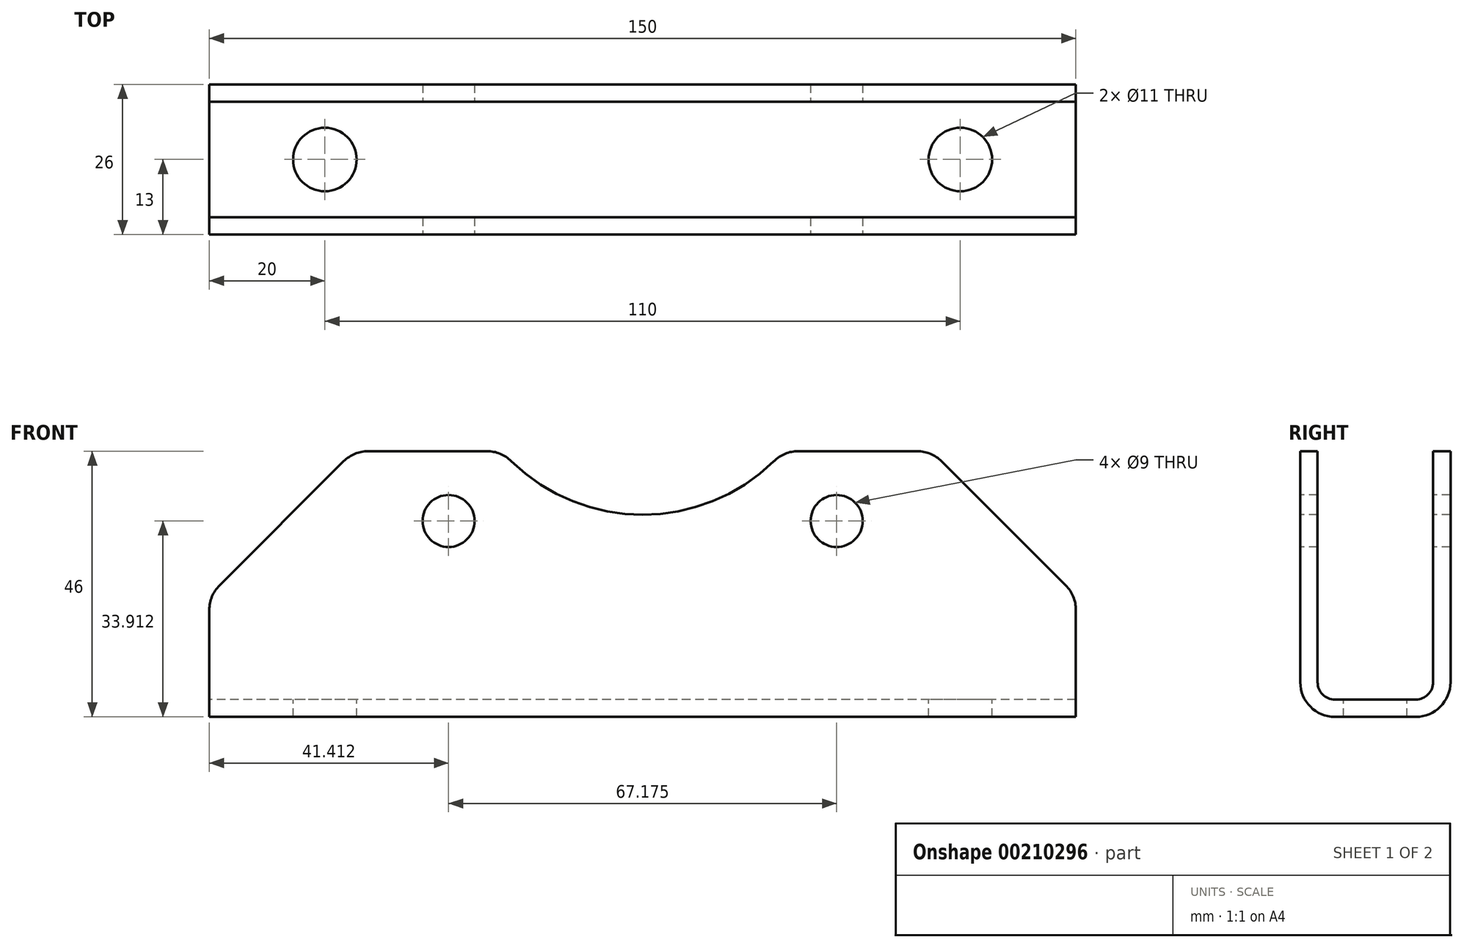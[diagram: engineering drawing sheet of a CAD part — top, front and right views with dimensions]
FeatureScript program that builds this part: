
annotation { "Feature Type Name" : "Feature", "Feature Type Description" : "" }
export const myFeature = defineFeature(function(context is Context, id is Id, definition is map)
    precondition{}
    {
        {
            var Q0;
            Q0=qCreatedBy(makeId("Right.planeOp"),FACE);
            var sketch = newSketch(context, id + "F0", { "sketchPlane" : qUnion([Q0])});
            skLineSegment(sketch, "E0.top", {"start": v(13, -23) * mm, "end": v(-13, -23) * mm});
            skLineSegment(sketch, "E0.left", {"start": v(13, 23) * mm, "end": v(13, -23) * mm});
            skLineSegment(sketch, "E0.right", {"start": v(-13, 23) * mm, "end": v(-13, -23) * mm});
            skPoint(sketch, "E0.middle", {"position": v(0, 0) * mm});
            skLineSegment(sketch, "E1.0", {"start": v(10, 23) * mm, "end": v(10, -20) * mm});
            skLineSegment(sketch, "E1.1", {"start": v(10, -20) * mm, "end": v(-10, -20) * mm});
            skLineSegment(sketch, "E1.2", {"start": v(-10, 23) * mm, "end": v(-10, -20) * mm});
            skLineSegment(sketch, "E2", {"start": v(-13, 23) * mm, "end": v(-10, 23) * mm});
            skLineSegment(sketch, "E3", {"start": v(10, 23) * mm, "end": v(13, 23) * mm});
            skSolve(sketch);
        }
        {
            var Q0;
            Q0=makeQuery(id+"F0.imprint","IMPRINT",FACE,{"disambiguationData":[TD([[makeQuery(id+"F0.imprint","IMPRINT",EDGE,{"derivedFrom":sQuery(id+"F0.wireOp",EDGE,"E0.top")}),-1.0]])]});
            extrude(context, id + "F1", {"entities" : qUnion([Q0]), "depth" : 150 * mm});
        }
        {
            var Q0;
            Q0=makeQuery(id+"F1.opExtrude","SWEPT_FACE",FACE,{"disambiguationData":[OSD([sQuery(id+"F0.wireOp",EDGE,"E0.right")])]});
            var sketch = newSketch(context, id + "F2", { "sketchPlane" : qUnion([Q0])});
            skLineSegment(sketch, "E4", {"start": v(27.5, 44.5) * mm, "end": v(122.5, 44.5) * mm, "construction": true});
            skLineSegment(sketch, "E5", {"start": v(75, -23) * mm, "end": v(75, 44.5) * mm, "construction": true});
            skCircle(sketch, "E6", {"center": v(75, 44.5) * mm, "radius": 32.5 * mm});
            skCircle(sketch, "E7", {"center": v(75, 44.5) * mm, "radius": 47.5 * mm, "construction": true});
            skLineSegment(sketch, "E8", {"start": v(75, 44.5) * mm, "end": v(41.41, 10.91) * mm, "construction": true});
            skLineSegment(sketch, "E9", {"start": v(75, 44.5) * mm, "end": v(108.59, 10.91) * mm, "construction": true});
            skCircle(sketch, "E10", {"center": v(108.59, 10.91) * mm, "radius": 4.5 * mm});
            skCircle(sketch, "E11", {"center": v(41.41, 10.91) * mm, "radius": 4.5 * mm});
            skSolve(sketch);
        }
        {
            var Q0;
            Q0 = qSketchRegion(id + "F2", true);
            extrude(context, id + "F3", {"entities" : qUnion([Q0]), "operationType" : NewBodyOperationType.REMOVE, "oppositeDirection" : true, "depth" : 50 * mm});
        }
        {
            var Q0;
            Q0=makeQuery(id+"F1.opExtrude","SWEPT_FACE",FACE,{"disambiguationData":[OSD([sQuery(id+"F0.wireOp",EDGE,"E1.1")])]});
            var sketch = newSketch(context, id + "F4", { "sketchPlane" : qUnion([Q0])});
            skLineSegment(sketch, "E12", {"start": v(0, 0) * mm, "end": v(150, 0) * mm, "construction": true});
            skLineSegment(sketch, "E13", {"start": v(20, 10) * mm, "end": v(20, -10) * mm, "construction": true});
            skLineSegment(sketch, "E14", {"start": v(130, 10) * mm, "end": v(130, -10) * mm, "construction": true});
            skCircle(sketch, "E15", {"center": v(20, 0) * mm, "radius": 5.5 * mm});
            skCircle(sketch, "E16", {"center": v(130, 0) * mm, "radius": 5.5 * mm});
            skSolve(sketch);
        }
        {
            var Q0;
            Q0 = qSketchRegion(id + "F4", true);
            extrude(context, id + "F5", {"entities" : qUnion([Q0]), "operationType" : NewBodyOperationType.REMOVE, "oppositeDirection" : true, "depth" : 25 * mm});
        }
        {
            var Q0;
            Q0=makeQuery(id+"F1.opExtrude","CAP_EDGE",EDGE,{"disambiguationData":[OSD([sQuery(id+"F0.wireOp",EDGE,"E3")])],"isStart":true});
            var Q1;
            Q1=makeQuery(id+"F1.opExtrude","CAP_EDGE",EDGE,{"disambiguationData":[OSD([sQuery(id+"F0.wireOp",EDGE,"E2")])],"isStart":true});
            var Q2;
            Q2=makeQuery(id+"F1.opExtrude","CAP_EDGE",EDGE,{"disambiguationData":[OSD([sQuery(id+"F0.wireOp",EDGE,"E2")])],"isStart":false});
            var Q3;
            Q3=makeQuery(id+"F1.opExtrude","CAP_EDGE",EDGE,{"disambiguationData":[OSD([sQuery(id+"F0.wireOp",EDGE,"E3")])],"isStart":false});
            chamfer(context, id + "F6", {"entities" : qUnion([Q0, Q1, Q2, Q3]), "width" : 25 * mm, "tangentPropagation" : true});
        }
        {
            var Q0;
            {var subQ0=sQuery(id+"F0.wireOp",EDGE,"E2");Q0=makeQuery(id+"F6.opChamfer","BLEND_EDGE",EDGE,{"blendedFrom":[makeQuery(id+"F1.opExtrude","CAP_EDGE",EDGE,{"disambiguationData":[OSD([subQ0])],"isStart":true}),makeQuery(id+"F1.opExtrude","CAP_FACE",FACE,{"disambiguationData":[OSD([sQuery(id+"F0.wireOp",EDGE,"E0.top"),sQuery(id+"F0.wireOp",EDGE,"E0.left"),sQuery(id+"F0.wireOp",EDGE,"E0.right"),sQuery(id+"F0.wireOp",EDGE,"E1.0"),sQuery(id+"F0.wireOp",EDGE,"E1.1"),sQuery(id+"F0.wireOp",EDGE,"E1.2"),subQ0,sQuery(id+"F0.wireOp",EDGE,"E3")])],"isStart":true})],"blendedInto":[makeQuery(id+"F1.opExtrude","CAP_FACE",FACE,{"disambiguationData":[OSD([sQuery(id+"F0.wireOp",EDGE,"E0.top"),sQuery(id+"F0.wireOp",EDGE,"E0.left"),sQuery(id+"F0.wireOp",EDGE,"E0.right"),sQuery(id+"F0.wireOp",EDGE,"E1.0"),sQuery(id+"F0.wireOp",EDGE,"E1.1"),sQuery(id+"F0.wireOp",EDGE,"E1.2"),subQ0,sQuery(id+"F0.wireOp",EDGE,"E3")])],"isStart":true})]});}
            var Q1;
            {var subQ0=sQuery(id+"F0.wireOp",EDGE,"E3");Q1=makeQuery(id+"F6.opChamfer","BLEND_EDGE",EDGE,{"blendedFrom":[makeQuery(id+"F1.opExtrude","CAP_EDGE",EDGE,{"disambiguationData":[OSD([subQ0])],"isStart":true}),makeQuery(id+"F1.opExtrude","CAP_FACE",FACE,{"disambiguationData":[OSD([sQuery(id+"F0.wireOp",EDGE,"E0.top"),sQuery(id+"F0.wireOp",EDGE,"E0.left"),sQuery(id+"F0.wireOp",EDGE,"E0.right"),sQuery(id+"F0.wireOp",EDGE,"E1.0"),sQuery(id+"F0.wireOp",EDGE,"E1.1"),sQuery(id+"F0.wireOp",EDGE,"E1.2"),sQuery(id+"F0.wireOp",EDGE,"E2"),subQ0])],"isStart":true})],"blendedInto":[makeQuery(id+"F1.opExtrude","CAP_FACE",FACE,{"disambiguationData":[OSD([sQuery(id+"F0.wireOp",EDGE,"E0.top"),sQuery(id+"F0.wireOp",EDGE,"E0.left"),sQuery(id+"F0.wireOp",EDGE,"E0.right"),sQuery(id+"F0.wireOp",EDGE,"E1.0"),sQuery(id+"F0.wireOp",EDGE,"E1.1"),sQuery(id+"F0.wireOp",EDGE,"E1.2"),sQuery(id+"F0.wireOp",EDGE,"E2"),subQ0])],"isStart":true})]});}
            var Q2;
            {var subQ0=sQuery(id+"F0.wireOp",EDGE,"E3");var subQ1=sQuery(id+"F0.wireOp",EDGE,"E1.0");var subQ2=sQuery(id+"F0.wireOp",EDGE,"E0.left");Q2=makeQuery(id+"F6.opChamfer","BLEND_EDGE",EDGE,{"blendedFrom":[makeQuery(id+"F1.opExtrude","CAP_EDGE",EDGE,{"disambiguationData":[OSD([subQ0])],"isStart":true}),makeQuery(id+"F3.boolean.opBoolean","SPLIT",FACE,{"disambiguationData":[TD([makeQuery(id+"F1.opExtrude","CAP_FACE",FACE,{"disambiguationData":[OSD([sQuery(id+"F0.wireOp",EDGE,"E0.top"),subQ2,sQuery(id+"F0.wireOp",EDGE,"E0.right"),subQ1,sQuery(id+"F0.wireOp",EDGE,"E1.1"),sQuery(id+"F0.wireOp",EDGE,"E1.2"),sQuery(id+"F0.wireOp",EDGE,"E2"),subQ0])],"isStart":true})])],"derivedFrom":makeQuery(id+"F1.opExtrude","SWEPT_FACE",FACE,{"disambiguationData":[OSD([subQ0])]})})],"blendedInto":[makeQuery(id+"F3.boolean.opBoolean","SPLIT",FACE,{"disambiguationData":[TD([makeQuery(id+"F1.opExtrude","CAP_FACE",FACE,{"disambiguationData":[OSD([sQuery(id+"F0.wireOp",EDGE,"E0.top"),subQ2,sQuery(id+"F0.wireOp",EDGE,"E0.right"),subQ1,sQuery(id+"F0.wireOp",EDGE,"E1.1"),sQuery(id+"F0.wireOp",EDGE,"E1.2"),sQuery(id+"F0.wireOp",EDGE,"E2"),subQ0])],"isStart":true})])],"derivedFrom":makeQuery(id+"F1.opExtrude","SWEPT_FACE",FACE,{"disambiguationData":[OSD([subQ0])]})})]});}
            var Q3;
            {var subQ0=sQuery(id+"F0.wireOp",EDGE,"E2");var subQ1=sQuery(id+"F0.wireOp",EDGE,"E1.2");var subQ2=sQuery(id+"F0.wireOp",EDGE,"E0.right");Q3=makeQuery(id+"F6.opChamfer","BLEND_EDGE",EDGE,{"blendedFrom":[makeQuery(id+"F1.opExtrude","CAP_EDGE",EDGE,{"disambiguationData":[OSD([subQ0])],"isStart":true}),makeQuery(id+"F3.boolean.opBoolean","SPLIT",FACE,{"disambiguationData":[TD([makeQuery(id+"F1.opExtrude","CAP_FACE",FACE,{"disambiguationData":[OSD([sQuery(id+"F0.wireOp",EDGE,"E0.top"),sQuery(id+"F0.wireOp",EDGE,"E0.left"),subQ2,sQuery(id+"F0.wireOp",EDGE,"E1.0"),sQuery(id+"F0.wireOp",EDGE,"E1.1"),subQ1,subQ0,sQuery(id+"F0.wireOp",EDGE,"E3")])],"isStart":true})])],"derivedFrom":makeQuery(id+"F1.opExtrude","SWEPT_FACE",FACE,{"disambiguationData":[OSD([subQ0])]})})],"blendedInto":[makeQuery(id+"F3.boolean.opBoolean","SPLIT",FACE,{"disambiguationData":[TD([makeQuery(id+"F1.opExtrude","CAP_FACE",FACE,{"disambiguationData":[OSD([sQuery(id+"F0.wireOp",EDGE,"E0.top"),sQuery(id+"F0.wireOp",EDGE,"E0.left"),subQ2,sQuery(id+"F0.wireOp",EDGE,"E1.0"),sQuery(id+"F0.wireOp",EDGE,"E1.1"),subQ1,subQ0,sQuery(id+"F0.wireOp",EDGE,"E3")])],"isStart":true})])],"derivedFrom":makeQuery(id+"F1.opExtrude","SWEPT_FACE",FACE,{"disambiguationData":[OSD([subQ0])]})})]});}
            var Q4;
            Q4=makeQuery(id+"F3.boolean.opBoolean","INTERSECT",EDGE,{"disambiguationData":[OD(0.0)],"derivedFrom":[makeQuery(id+"F1.opExtrude","SWEPT_FACE",FACE,{"disambiguationData":[OSD([sQuery(id+"F0.wireOp",EDGE,"E2")])]}),makeQuery(id+"F3.opExtrude","SWEPT_FACE",FACE,{"disambiguationData":[OSD([sQuery(id+"F2.wireOp",EDGE,"E6")])]})]});
            var Q5;
            Q5=makeQuery(id+"F3.boolean.opBoolean","INTERSECT",EDGE,{"disambiguationData":[OD(0.0)],"derivedFrom":[makeQuery(id+"F1.opExtrude","SWEPT_FACE",FACE,{"disambiguationData":[OSD([sQuery(id+"F0.wireOp",EDGE,"E3")])]}),makeQuery(id+"F3.opExtrude","SWEPT_FACE",FACE,{"disambiguationData":[OSD([sQuery(id+"F2.wireOp",EDGE,"E6")])]})]});
            var Q6;
            Q6=makeQuery(id+"F3.boolean.opBoolean","INTERSECT",EDGE,{"disambiguationData":[OD(1.0)],"derivedFrom":[makeQuery(id+"F1.opExtrude","SWEPT_FACE",FACE,{"disambiguationData":[OSD([sQuery(id+"F0.wireOp",EDGE,"E3")])]}),makeQuery(id+"F3.opExtrude","SWEPT_FACE",FACE,{"disambiguationData":[OSD([sQuery(id+"F2.wireOp",EDGE,"E6")])]})]});
            var Q7;
            Q7=makeQuery(id+"F3.boolean.opBoolean","INTERSECT",EDGE,{"disambiguationData":[OD(1.0)],"derivedFrom":[makeQuery(id+"F1.opExtrude","SWEPT_FACE",FACE,{"disambiguationData":[OSD([sQuery(id+"F0.wireOp",EDGE,"E2")])]}),makeQuery(id+"F3.opExtrude","SWEPT_FACE",FACE,{"disambiguationData":[OSD([sQuery(id+"F2.wireOp",EDGE,"E6")])]})]});
            var Q8;
            {var subQ0=sQuery(id+"F0.wireOp",EDGE,"E2");var subQ1=sQuery(id+"F0.wireOp",EDGE,"E1.2");var subQ2=sQuery(id+"F0.wireOp",EDGE,"E0.right");Q8=makeQuery(id+"F6.opChamfer","BLEND_EDGE",EDGE,{"blendedFrom":[makeQuery(id+"F1.opExtrude","CAP_EDGE",EDGE,{"disambiguationData":[OSD([subQ0])],"isStart":false}),makeQuery(id+"F3.boolean.opBoolean","SPLIT",FACE,{"disambiguationData":[TD([makeQuery(id+"F1.opExtrude","CAP_FACE",FACE,{"disambiguationData":[OSD([sQuery(id+"F0.wireOp",EDGE,"E0.top"),sQuery(id+"F0.wireOp",EDGE,"E0.left"),subQ2,sQuery(id+"F0.wireOp",EDGE,"E1.0"),sQuery(id+"F0.wireOp",EDGE,"E1.1"),subQ1,subQ0,sQuery(id+"F0.wireOp",EDGE,"E3")])],"isStart":false})])],"derivedFrom":makeQuery(id+"F1.opExtrude","SWEPT_FACE",FACE,{"disambiguationData":[OSD([subQ0])]})})],"blendedInto":[makeQuery(id+"F3.boolean.opBoolean","SPLIT",FACE,{"disambiguationData":[TD([makeQuery(id+"F1.opExtrude","CAP_FACE",FACE,{"disambiguationData":[OSD([sQuery(id+"F0.wireOp",EDGE,"E0.top"),sQuery(id+"F0.wireOp",EDGE,"E0.left"),subQ2,sQuery(id+"F0.wireOp",EDGE,"E1.0"),sQuery(id+"F0.wireOp",EDGE,"E1.1"),subQ1,subQ0,sQuery(id+"F0.wireOp",EDGE,"E3")])],"isStart":false})])],"derivedFrom":makeQuery(id+"F1.opExtrude","SWEPT_FACE",FACE,{"disambiguationData":[OSD([subQ0])]})})]});}
            var Q9;
            {var subQ0=sQuery(id+"F0.wireOp",EDGE,"E3");var subQ1=sQuery(id+"F0.wireOp",EDGE,"E1.0");var subQ2=sQuery(id+"F0.wireOp",EDGE,"E0.left");Q9=makeQuery(id+"F6.opChamfer","BLEND_EDGE",EDGE,{"blendedFrom":[makeQuery(id+"F1.opExtrude","CAP_EDGE",EDGE,{"disambiguationData":[OSD([subQ0])],"isStart":false}),makeQuery(id+"F3.boolean.opBoolean","SPLIT",FACE,{"disambiguationData":[TD([makeQuery(id+"F1.opExtrude","CAP_FACE",FACE,{"disambiguationData":[OSD([sQuery(id+"F0.wireOp",EDGE,"E0.top"),subQ2,sQuery(id+"F0.wireOp",EDGE,"E0.right"),subQ1,sQuery(id+"F0.wireOp",EDGE,"E1.1"),sQuery(id+"F0.wireOp",EDGE,"E1.2"),sQuery(id+"F0.wireOp",EDGE,"E2"),subQ0])],"isStart":false})])],"derivedFrom":makeQuery(id+"F1.opExtrude","SWEPT_FACE",FACE,{"disambiguationData":[OSD([subQ0])]})})],"blendedInto":[makeQuery(id+"F3.boolean.opBoolean","SPLIT",FACE,{"disambiguationData":[TD([makeQuery(id+"F1.opExtrude","CAP_FACE",FACE,{"disambiguationData":[OSD([sQuery(id+"F0.wireOp",EDGE,"E0.top"),subQ2,sQuery(id+"F0.wireOp",EDGE,"E0.right"),subQ1,sQuery(id+"F0.wireOp",EDGE,"E1.1"),sQuery(id+"F0.wireOp",EDGE,"E1.2"),sQuery(id+"F0.wireOp",EDGE,"E2"),subQ0])],"isStart":false})])],"derivedFrom":makeQuery(id+"F1.opExtrude","SWEPT_FACE",FACE,{"disambiguationData":[OSD([subQ0])]})})]});}
            var Q10;
            {var subQ0=sQuery(id+"F0.wireOp",EDGE,"E3");Q10=makeQuery(id+"F6.opChamfer","BLEND_EDGE",EDGE,{"blendedFrom":[makeQuery(id+"F1.opExtrude","CAP_EDGE",EDGE,{"disambiguationData":[OSD([subQ0])],"isStart":false}),makeQuery(id+"F1.opExtrude","CAP_FACE",FACE,{"disambiguationData":[OSD([sQuery(id+"F0.wireOp",EDGE,"E0.top"),sQuery(id+"F0.wireOp",EDGE,"E0.left"),sQuery(id+"F0.wireOp",EDGE,"E0.right"),sQuery(id+"F0.wireOp",EDGE,"E1.0"),sQuery(id+"F0.wireOp",EDGE,"E1.1"),sQuery(id+"F0.wireOp",EDGE,"E1.2"),sQuery(id+"F0.wireOp",EDGE,"E2"),subQ0])],"isStart":false})],"blendedInto":[makeQuery(id+"F1.opExtrude","CAP_FACE",FACE,{"disambiguationData":[OSD([sQuery(id+"F0.wireOp",EDGE,"E0.top"),sQuery(id+"F0.wireOp",EDGE,"E0.left"),sQuery(id+"F0.wireOp",EDGE,"E0.right"),sQuery(id+"F0.wireOp",EDGE,"E1.0"),sQuery(id+"F0.wireOp",EDGE,"E1.1"),sQuery(id+"F0.wireOp",EDGE,"E1.2"),sQuery(id+"F0.wireOp",EDGE,"E2"),subQ0])],"isStart":false})]});}
            var Q11;
            {var subQ0=sQuery(id+"F0.wireOp",EDGE,"E2");Q11=makeQuery(id+"F6.opChamfer","BLEND_EDGE",EDGE,{"blendedFrom":[makeQuery(id+"F1.opExtrude","CAP_EDGE",EDGE,{"disambiguationData":[OSD([subQ0])],"isStart":false}),makeQuery(id+"F1.opExtrude","CAP_FACE",FACE,{"disambiguationData":[OSD([sQuery(id+"F0.wireOp",EDGE,"E0.top"),sQuery(id+"F0.wireOp",EDGE,"E0.left"),sQuery(id+"F0.wireOp",EDGE,"E0.right"),sQuery(id+"F0.wireOp",EDGE,"E1.0"),sQuery(id+"F0.wireOp",EDGE,"E1.1"),sQuery(id+"F0.wireOp",EDGE,"E1.2"),subQ0,sQuery(id+"F0.wireOp",EDGE,"E3")])],"isStart":false})],"blendedInto":[makeQuery(id+"F1.opExtrude","CAP_FACE",FACE,{"disambiguationData":[OSD([sQuery(id+"F0.wireOp",EDGE,"E0.top"),sQuery(id+"F0.wireOp",EDGE,"E0.left"),sQuery(id+"F0.wireOp",EDGE,"E0.right"),sQuery(id+"F0.wireOp",EDGE,"E1.0"),sQuery(id+"F0.wireOp",EDGE,"E1.1"),sQuery(id+"F0.wireOp",EDGE,"E1.2"),subQ0,sQuery(id+"F0.wireOp",EDGE,"E3")])],"isStart":false})]});}
            var Q12;
            Q12=makeQuery(id+"F1.opExtrude","SWEPT_EDGE",EDGE,{"disambiguationData":[OSD([sQuery(id+"F0.wireOp",EDGE,"E0.top"),sQuery(id+"F0.wireOp",EDGE,"E0.right")])]});
            var Q13;
            Q13=makeQuery(id+"F1.opExtrude","SWEPT_EDGE",EDGE,{"disambiguationData":[OSD([sQuery(id+"F0.wireOp",EDGE,"E0.top"),sQuery(id+"F0.wireOp",EDGE,"E0.left")])]});
            fillet(context, id + "F7", {"entities" : qUnion([Q0, Q1, Q2, Q3, Q4, Q5, Q6, Q7, Q8, Q9, Q10, Q11, Q12, Q13]), "radius" : 6 * mm, "tangentPropagation" : true, "allowEdgeOverflow" : false});
        }
        {
            var Q0;
            Q0 = qSketchRegion(id + "F2", true);
            extrude(context, id + "F8", {"entities" : qUnion([Q0]), "operationType" : NewBodyOperationType.REMOVE, "oppositeDirection" : true, "depth" : 25 * mm});
        }
        {
            var Q0;
            Q0=makeQuery(id+"F1.opExtrude","SWEPT_EDGE",EDGE,{"disambiguationData":[OSD([sQuery(id+"F0.wireOp",EDGE,"E1.0"),sQuery(id+"F0.wireOp",EDGE,"E1.1")])]});
            var Q1;
            Q1=makeQuery(id+"F1.opExtrude","SWEPT_EDGE",EDGE,{"disambiguationData":[OSD([sQuery(id+"F0.wireOp",EDGE,"E1.1"),sQuery(id+"F0.wireOp",EDGE,"E1.2")])]});
            fillet(context, id + "F9", {"entities" : qUnion([Q0, Q1]), "radius" : 3 * mm, "tangentPropagation" : true, "allowEdgeOverflow" : false});
        }
    });
